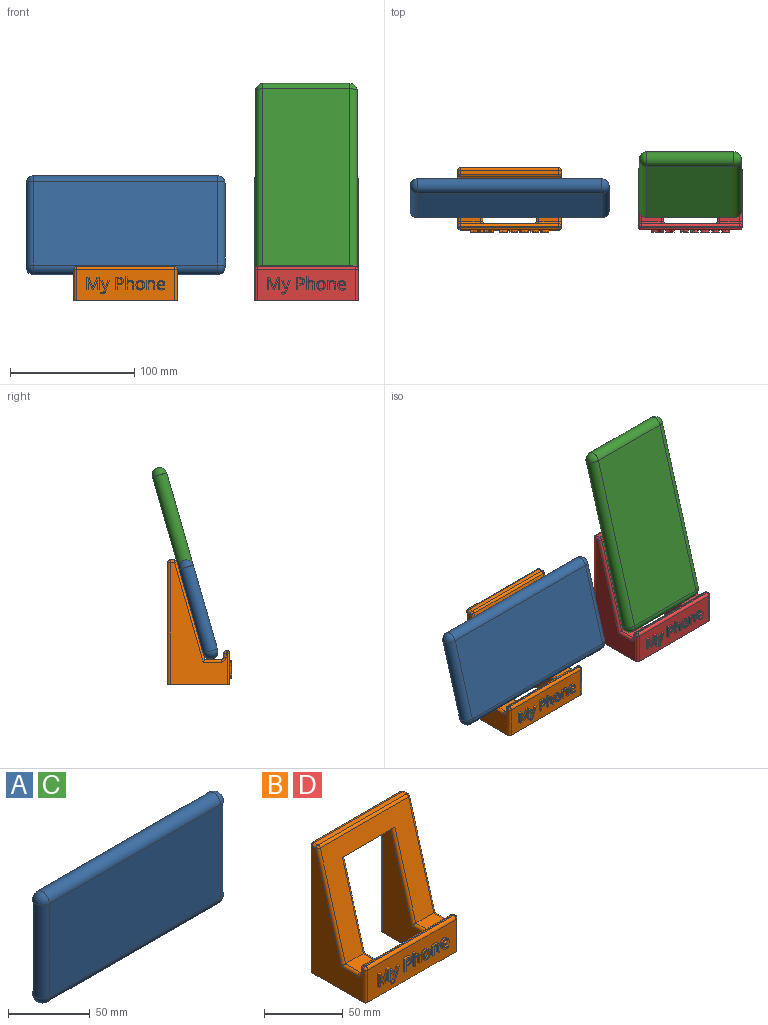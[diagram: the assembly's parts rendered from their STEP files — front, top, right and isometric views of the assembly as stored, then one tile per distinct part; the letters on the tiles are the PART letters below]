
ASSEMBLY  parts=4 mates=2
PART A: 10 faces, bbox 160x12x82 mm
  f0: plane 148x70mm, normal (0,-1,0), area 10360mm2, adj f3,f4,f7,f8
  f1: plane 148x70mm, normal (0,1,0), area 10360mm2, adj f3,f4,f7,f8
  f2: sphere r=6mm, area 113.1mm2, adj f3,f4
  f3: cylinder r=6mm len=148mm, axis (1,0,0), area 2789.7mm2, adj f0,f1,f2,f5
  f4: cylinder r=6mm len=70mm, axis (0,0,-1), area 1319.5mm2, adj f0,f1,f2,f6
  f5: sphere r=6mm, area 113.1mm2, adj f3,f7
  f6: sphere r=6mm, area 113.1mm2, adj f4,f8
  f7: cylinder r=6mm len=70mm, axis (0,0,1), area 1319.5mm2, adj f0,f1,f5,f9
  f8: cylinder r=6mm len=148mm, axis (-1,0,0), area 2789.7mm2, adj f0,f1,f6,f9
  f9: sphere r=6mm, area 113.1mm2, adj f7,f8
PART B: 184 faces, bbox 83x51.7x100 mm
  f0: plane 79x25mm, normal (0,-1,0), area 1757.8mm2, adj f2,f14,f15,f16,f17,f18,f19,f20
  f1: plane 16x13mm, normal (0,0,1), area 208mm2, adj f3,f175,f178,f181
  f2: plane 83x50mm, normal (0,0,-1), area 2211.6mm2, adj f0,f5,f6,f7,f10,f11,f12,f146
  f3: plane 79x78.55mm, normal (0,-0.96,0.28), area 3278.3mm2, adj f1,f4,f13,f144,f153,f165,f172,f174
  f4: plane 16x13mm, normal (0,0,1), area 208mm2, adj f3,f145,f151,f152
  f5: plane 98x79mm, normal (0,1,0), area 3747mm2, adj f2,f13,f147,f155,f156,f182,f183
  f6: plane 98x46mm, normal (1,0,0), area 2038mm2, adj f2,f156,f161,f166,f170,f172,f175,f176
  f7: plane 98x46mm, normal (-1,0,0), area 2038mm2, adj f2,f147,f149,f151,f153,f154,f158,f163
  f8: plane 79x3.49mm, normal (0,0,1), area 276mm2, adj f154,f155,f165,f166
  f9: plane 79x1mm, normal (0,0,1), area 79mm2, adj f162,f163,f170,f171
  f10: plane 79x25mm, normal (0,1,0), area 1101.9mm2, adj f2,f146,f150,f152,f164,f171,f176,f177
  f11: plane 85x41mm, normal (-1,0,0), area 1867.8mm2, adj f2,f13,f174,f177,f178,f183
  f12: plane 85x41mm, normal (1,0,0), area 1867.8mm2, adj f2,f13,f144,f145,f146,f182
  f13: plane 47x11.31mm, normal (0,0,-1), area 489.9mm2, adj f3,f5,f11,f12,f144,f174,f182,f183
  f14: plane 8.79x3.36mm, normal (-0.93,0,-0.36), area 16mm2, adj f0,f15,f31,f32
  f15: plane 1.7x0.93mm, normal (0,0,-1), area 1.6mm2, adj f0,f14,f16,f32
  f16: plane 8.78x3.39mm, normal (0.93,0,-0.36), area 16mm2, adj f0,f15,f17,f32
  f17: plane 1.7x0.05mm, normal (0,0,-1), area 0.1mm2, adj f0,f16,f18,f32
  f18: extruded ~2.39x1.7mm, area 4.1mm2, adj f0,f17,f19,f32
  f19: plane 6.39x1.7mm, normal (-1,0,0), area 10.9mm2, adj f0,f18,f20,f32
  f20: plane 1.7x1.15mm, normal (0,0,-1), area 2mm2, adj f0,f19,f21,f32
  f21: plane 9.92x1.7mm, normal (1,0,0), area 16.9mm2, adj f0,f20,f22,f32
  f22: plane 1.72x1.7mm, normal (0,0,1), area 2.9mm2, adj f0,f21,f23,f32
  f23: plane 8.18x3.17mm, normal (-0.93,0,0.36), area 14.9mm2, adj f0,f22,f24,f32
  f24: plane 1.7x0.05mm, normal (0,0,1), area 0.1mm2, adj f0,f23,f25,f32
  f25: plane 8.18x3.14mm, normal (0.93,0,0.36), area 14.9mm2, adj f0,f24,f26,f32
  f26: plane 1.74x1.7mm, normal (0,0,1), area 3mm2, adj f0,f25,f27,f32
  f27: plane 9.92x1.7mm, normal (-1,0,0), area 16.9mm2, adj f0,f26,f28,f32
  f28: plane 1.7x1.07mm, normal (0,0,-1), area 1.8mm2, adj f0,f27,f29,f32
  f29: plane 6.31x1.7mm, normal (1,0,0), area 10.7mm2, adj f0,f28,f30,f32
  f30: extruded ~2.48x1.7mm, area 4.2mm2, adj f0,f29,f31,f32
  f31: plane 1.7x0.05mm, normal (0,0,-1), area 0.1mm2, adj f0,f14,f30,f32
  f32: plane 9.92x9.82mm, normal (0,-1,0), area 42mm2, adj f14,f15,f16,f17,f18,f19,f20,f21
  f33: plane 1.7x1.21mm, normal (0,0,1), area 2.1mm2, adj f0,f34,f48,f49
  f34: plane 7.47x3mm, normal (-0.93,0,-0.37), area 13.7mm2, adj f0,f33,f35,f49
  f35: plane 1.7x1.06mm, normal (-0.93,0,0.37), area 1.9mm2, adj f0,f34,f36,f49
  f36: extruded ~1.7x1.66mm, area 3.8mm2, adj f0,f35,f37,f49
  f37: extruded ~1.7x0.83mm, area 1.4mm2, adj f0,f36,f38,f49
  f38: plane 1.7x0.9mm, normal (-1,0,0), area 1.5mm2, adj f0,f37,f39,f49
  f39: extruded ~1.7x1.02mm, area 1.7mm2, adj f0,f38,f40,f49
  f40: extruded ~1.7x1.56mm, area 2.9mm2, adj f0,f39,f41,f49
  f41: extruded ~1.78x1.7mm, area 3.6mm2, adj f0,f40,f42,f49
  f42: plane 8.46x3.19mm, normal (0.94,0,-0.35), area 15.4mm2, adj f0,f41,f43,f49
  f43: plane 1.7x1.21mm, normal (0,0,1), area 2.1mm2, adj f0,f42,f44,f49
  f44: extruded ~5.15x1.84mm, area 9.3mm2, adj f0,f43,f45,f49
  f45: extruded ~1.7x1.19mm, area 2.1mm2, adj f0,f44,f46,f49
  f46: plane 1.7x0.05mm, normal (0,0,1), area 0.1mm2, adj f0,f45,f47,f49
  f47: extruded ~2.1x1.7mm, area 3.7mm2, adj f0,f46,f48,f49
  f48: plane 4.24x1.7mm, normal (0.93,0,0.36), area 7.7mm2, adj f0,f33,f47,f49
  f49: plane 10.77x6.97mm, normal (0,-1,0), area 21.4mm2, adj f33,f34,f35,f36,f37,f38,f39,f40
  f50: plane 1.7x1.04mm, normal (0,0,1), area 1.8mm2, adj f51,f64,f65,f66
  f51: plane 4.03x1.7mm, normal (1,0,0), area 6.8mm2, adj f50,f52,f65,f66
  f52: plane 1.7x1.29mm, normal (0,0,-1), area 2.2mm2, adj f51,f53,f65,f66
  f53: extruded ~2.01x1.7mm, area 3.6mm2, adj f52,f54,f65,f66
  f54: extruded ~1.7x1.46mm, area 2.8mm2, adj f53,f55,f65,f66
  f55: extruded ~1.7x1.59mm, area 3.1mm2, adj f54,f64,f65,f66
  f56: extruded ~2.32x1.7mm, area 4.5mm2, adj f0,f57,f63,f65
  f57: extruded ~3.72x2.89mm, area 9.1mm2, adj f0,f56,f58,f65
  f58: plane 2.57x1.7mm, normal (0,0,1), area 4.4mm2, adj f0,f57,f59,f65
  f59: plane 9.92x1.7mm, normal (-1,0,0), area 16.9mm2, adj f0,f58,f60,f65
  f60: plane 1.7x1.15mm, normal (0,0,-1), area 2mm2, adj f0,f59,f61,f65
  f61: plane 3.9x1.7mm, normal (1,0,0), area 6.6mm2, adj f0,f60,f62,f65
  f62: plane 1.7x1.17mm, normal (0,0,-1), area 2mm2, adj f0,f61,f63,f65
  f63: extruded ~2.94x1.7mm, area 5.3mm2, adj f0,f56,f62,f65
  f64: extruded ~2.22x1.7mm, area 3.9mm2, adj f50,f55,f65,f66
  f65: plane 9.92x6.29mm, normal (0,-1,0), area 24.2mm2, adj f50,f51,f52,f53,f54,f55,f56,f57
  f66: plane 4.03x3.94mm, normal (0,-1,0), area 14.1mm2, adj f50,f51,f52,f53,f54,f55,f64
  f67: plane 4.81x1.7mm, normal (-1,0,0), area 8.2mm2, adj f0,f68,f84,f85
  f68: plane 1.7x1.13mm, normal (0,0,-1), area 1.9mm2, adj f0,f67,f69,f85
  f69: plane 4.85x1.7mm, normal (1,0,0), area 8.2mm2, adj f0,f68,f70,f85
  f70: extruded ~2.06x1.7mm, area 3.8mm2, adj f0,f69,f71,f85
  f71: extruded ~2.05x1.7mm, area 3.7mm2, adj f0,f70,f72,f85
  f72: extruded ~1.7x1.4mm, area 2.5mm2, adj f0,f71,f73,f85
  f73: extruded ~1.7x0.95mm, area 2.2mm2, adj f0,f72,f74,f85
  f74: plane 1.7x0.07mm, normal (0,0,1), area 0.1mm2, adj f0,f73,f75,f85
  f75: extruded ~1.7x0.96mm, area 1.6mm2, adj f0,f74,f76,f85
  f76: plane 3.19x1.7mm, normal (1,0,0), area 5.4mm2, adj f0,f75,f77,f85
  f77: plane 1.7x1.13mm, normal (0,0,1), area 1.9mm2, adj f0,f76,f78,f85
  f78: plane 10.55x1.7mm, normal (-1,0,0), area 17.9mm2, adj f0,f77,f79,f85
  f79: plane 1.7x1.13mm, normal (0,0,-1), area 1.9mm2, adj f0,f78,f80,f85
  f80: plane 3.89x1.7mm, normal (1,0,0), area 6.6mm2, adj f0,f79,f81,f85
  f81: extruded ~2.09x1.7mm, area 3.7mm2, adj f0,f80,f82,f85
  f82: extruded ~1.71x1.7mm, area 3.2mm2, adj f0,f81,f83,f85
  f83: extruded ~1.7x1.3mm, area 2.4mm2, adj f0,f82,f84,f85
  f84: extruded ~1.7x1.36mm, area 2.5mm2, adj f0,f67,f83,f85
  f85: plane 10.55x6.21mm, normal (0,-1,0), area 23.6mm2, adj f67,f68,f69,f70,f71,f72,f73,f74
  f86: extruded ~2.17x1.7mm, area 3.9mm2, adj f87,f102,f103,f104
  f87: extruded ~2.16x1.7mm, area 3.9mm2, adj f86,f88,f103,f104
  f88: extruded ~1.7x1.67mm, area 3.2mm2, adj f87,f89,f103,f104
  f89: extruded ~1.7x1.69mm, area 3.3mm2, adj f88,f90,f103,f104
  f90: extruded ~2.15x1.7mm, area 3.9mm2, adj f89,f91,f103,f104
  f91: extruded ~2.17x1.7mm, area 3.9mm2, adj f90,f92,f103,f104
  f92: extruded ~1.7x1.68mm, area 3.2mm2, adj f91,f102,f103,f104
  f93: extruded ~2.84x1.7mm, area 5.2mm2, adj f0,f94,f101,f103
  f94: extruded ~2.81x1.7mm, area 5.1mm2, adj f0,f93,f95,f103
  f95: extruded ~2.48x1.7mm, area 4.7mm2, adj f0,f94,f96,f103
  f96: extruded ~2.52x1.7mm, area 4.8mm2, adj f0,f95,f97,f103
  f97: extruded ~2.83x1.7mm, area 5.2mm2, adj f0,f96,f98,f103
  f98: extruded ~2.05x1.7mm, area 3.6mm2, adj f0,f97,f99,f103
  f99: extruded ~1.7x1.34mm, area 3.1mm2, adj f0,f98,f100,f103
  f100: extruded ~1.77x1.7mm, area 3.2mm2, adj f0,f99,f101,f103
  f101: extruded ~2.53x1.7mm, area 4.8mm2, adj f0,f93,f100,f103
  f102: extruded ~1.7x1.67mm, area 3.2mm2, adj f86,f92,f103,f104
  f103: plane 7.71x6.83mm, normal (0,-1,0), area 21.2mm2, adj f86,f87,f88,f89,f90,f91,f92,f93
  f104: plane 5.81x4.5mm, normal (0,-1,0), area 21.7mm2, adj f86,f87,f88,f89,f90,f91,f92,f102
  f105: plane 4.81x1.7mm, normal (-1,0,0), area 8.2mm2, adj f0,f106,f121,f122
  f106: plane 1.7x1.13mm, normal (0,0,-1), area 1.9mm2, adj f0,f105,f107,f122
  f107: plane 4.85x1.7mm, normal (1,0,0), area 8.2mm2, adj f0,f106,f108,f122
  f108: extruded ~2.07x1.7mm, area 3.8mm2, adj f0,f107,f109,f122
  f109: extruded ~2.02x1.7mm, area 3.7mm2, adj f0,f108,f110,f122
  f110: extruded ~1.7x1.39mm, area 2.4mm2, adj f0,f109,f111,f122
  f111: extruded ~1.7x0.97mm, area 2.2mm2, adj f0,f110,f112,f122
  f112: plane 1.7x0.05mm, normal (0,0,1), area 0.1mm2, adj f0,f111,f113,f122
  f113: plane 1.7x1.02mm, normal (0.98,0,0.18), area 1.8mm2, adj f0,f112,f114,f122
  f114: plane 1.7x0.92mm, normal (0,0,1), area 1.6mm2, adj f0,f113,f115,f122
  f115: plane 7.43x1.7mm, normal (-1,0,0), area 12.6mm2, adj f0,f114,f116,f122
  f116: plane 1.7x1.13mm, normal (0,0,-1), area 1.9mm2, adj f0,f115,f117,f122
  f117: plane 3.9x1.7mm, normal (1,0,0), area 6.6mm2, adj f0,f116,f118,f122
  f118: extruded ~2.08x1.7mm, area 3.7mm2, adj f0,f117,f119,f122
  f119: extruded ~1.71x1.7mm, area 3.2mm2, adj f0,f118,f120,f122
  f120: extruded ~1.7x1.3mm, area 2.4mm2, adj f0,f119,f121,f122
  f121: extruded ~1.7x1.36mm, area 2.5mm2, adj f0,f105,f120,f122
  f122: plane 7.57x6.21mm, normal (0,-1,0), area 20mm2, adj f105,f106,f107,f108,f109,f110,f111,f112
  f123: extruded ~1.7x1.43mm, area 2.7mm2, adj f124,f141,f142,f143
  f124: extruded ~1.7x1.36mm, area 2.6mm2, adj f123,f125,f142,f143
  f125: extruded ~1.7x1.63mm, area 2.9mm2, adj f124,f126,f142,f143
  f126: plane 3.89x1.7mm, normal (0,0,1), area 6.6mm2, adj f125,f141,f142,f143
  f127: extruded ~2.6x1.7mm, area 4.9mm2, adj f0,f128,f140,f142
  f128: extruded ~1.7x1.28mm, area 2.2mm2, adj f0,f127,f129,f142
  f129: extruded ~1.7x1.13mm, area 2mm2, adj f0,f128,f130,f142
  f130: plane 1.7x1mm, normal (1,0,0), area 1.7mm2, adj f0,f129,f131,f142
  f131: extruded ~2.37x1.7mm, area 4.2mm2, adj f0,f130,f132,f142
  f132: extruded ~1.77x1.7mm, area 3.3mm2, adj f0,f131,f133,f142
  f133: extruded ~1.99x1.7mm, area 3.6mm2, adj f0,f132,f134,f142
  f134: plane 5.12x1.7mm, normal (0,0,-1), area 8.7mm2, adj f0,f133,f135,f142
  f135: plane 1.7x0.71mm, normal (1,0,0), area 1.2mm2, adj f0,f134,f136,f142
  f136: extruded ~2.43x1.7mm, area 4.4mm2, adj f0,f135,f137,f142
  f137: extruded ~2.21x1.7mm, area 4.2mm2, adj f0,f136,f138,f142
  f138: extruded ~2.38x1.7mm, area 4.6mm2, adj f0,f137,f139,f142
  f139: extruded ~2.86x1.7mm, area 5.2mm2, adj f0,f138,f140,f142
  f140: extruded ~2.79x1.7mm, area 5.1mm2, adj f0,f127,f139,f142
  f141: extruded ~1.7x1.61mm, area 3mm2, adj f123,f126,f142,f143
  f142: plane 7.71x6.29mm, normal (0,-1,0), area 22mm2, adj f123,f124,f125,f126,f127,f128,f129,f130
  f143: plane 3.89x2.2mm, normal (0,-1,0), area 6.9mm2, adj f123,f124,f125,f126,f141
  f144: cylinder r=2mm len=67.55mm, axis (0,0.28,0.96), area 214.9mm2, adj f3,f12,f13,f145
  f145: cylinder r=2mm len=14.51mm, axis (0,1,0), area 42.6mm2, adj f4,f12,f144,f150
  f146: cylinder r=2mm len=18mm, axis (0,0,-1), area 56.5mm2, adj f2,f10,f12,f150
  f147: cylinder r=2mm len=98mm, axis (0,0,1), area 307.9mm2, adj f2,f5,f7,f148
  f148: sphere r=2mm, area 6.3mm2, adj f147,f154,f155
  f149: cylinder r=2mm len=25mm, axis (0,0,-1), area 78.5mm2, adj f0,f2,f7,f157
  f150: torus R=4mm, axis (0,-1,0), area 13.5mm2, adj f10,f145,f146,f152
  f151: cylinder r=2mm len=14.51mm, axis (0,-1,0), area 42.6mm2, adj f4,f7,f153,f158
  f152: cylinder r=2mm len=16mm, axis (1,0,0), area 50.3mm2, adj f4,f10,f150,f158
  f153: cylinder r=2mm len=80.55mm, axis (0,-0.28,-0.96), area 258.5mm2, adj f3,f7,f151,f159
  f154: cylinder r=2mm len=3.49mm, axis (0,-1,0), area 11mm2, adj f7,f8,f148,f159
  f155: cylinder r=2mm len=79mm, axis (-1,0,0), area 248.2mm2, adj f5,f8,f148,f160
  f156: cylinder r=2mm len=98mm, axis (0,0,-1), area 307.9mm2, adj f2,f5,f6,f160
  f157: sphere r=2mm, area 6.3mm2, adj f149,f162,f163
  f158: torus R=4mm, axis (1,0,0), area 13.5mm2, adj f7,f151,f152,f164
  f159: sphere r=2mm, area 5.2mm2, adj f153,f154,f165
  f160: sphere r=2mm, area 6.3mm2, adj f155,f156,f166
  f161: cylinder r=2mm len=25mm, axis (0,0,1), area 78.5mm2, adj f0,f2,f6,f167
  f162: cylinder r=2mm len=79mm, axis (-1,0,0), area 248.2mm2, adj f0,f9,f157,f167
  f163: cylinder r=2mm len=2mm, axis (0,-1,0), area 3.1mm2, adj f7,f9,f157,f168
  f164: cylinder r=2mm len=3mm, axis (0,0,1), area 9.4mm2, adj f7,f10,f158,f168
  f165: cylinder r=2mm len=79mm, axis (-1,0,0), area 204mm2, adj f3,f8,f159,f169
  f166: cylinder r=2mm len=3.49mm, axis (0,1,0), area 11mm2, adj f6,f8,f160,f169
  f167: sphere r=2mm, area 6.3mm2, adj f161,f162,f170
  f168: sphere r=2mm, area 6.3mm2, adj f163,f164,f171
  f169: sphere r=2mm, area 5.2mm2, adj f165,f166,f172
  f170: cylinder r=2mm len=2mm, axis (0,1,0), area 3.1mm2, adj f6,f9,f167,f173
  f171: cylinder r=2mm len=79mm, axis (1,0,0), area 248.2mm2, adj f9,f10,f168,f173
  f172: cylinder r=2mm len=80.55mm, axis (0,0.28,0.96), area 258.5mm2, adj f3,f6,f169,f175
  f173: sphere r=2mm, area 6.3mm2, adj f170,f171,f176
  f174: cylinder r=2mm len=67.55mm, axis (0,-0.28,-0.96), area 214.9mm2, adj f3,f11,f13,f178
  f175: cylinder r=2mm len=14.51mm, axis (0,1,0), area 42.6mm2, adj f1,f6,f172,f179
  f176: cylinder r=2mm len=3mm, axis (0,0,-1), area 9.4mm2, adj f6,f10,f173,f179
  f177: cylinder r=2mm len=18mm, axis (0,0,1), area 56.5mm2, adj f2,f10,f11,f180
  f178: cylinder r=2mm len=14.51mm, axis (0,-1,0), area 42.6mm2, adj f1,f11,f174,f180
  f179: torus R=4mm, axis (1,0,0), area 13.5mm2, adj f6,f175,f176,f181
  f180: torus R=4mm, axis (0,-1,0), area 13.5mm2, adj f10,f177,f178,f181
  f181: cylinder r=2mm len=16mm, axis (1,0,0), area 50.3mm2, adj f1,f10,f179,f180
  f182: cylinder r=2mm len=85mm, axis (0,0,1), area 267mm2, adj f2,f5,f12,f13
  f183: cylinder r=2mm len=85mm, axis (0,0,-1), area 267mm2, adj f2,f5,f11,f13
PART C: same geometry as A
PART D: same geometry as B
PLACE A rot(axis=(-1,0,0),16deg) t=(-39.91,-5.17,2.31)mm
PLACE B t=(-39.91,25.01,-17.05)mm
PLACE C rot(axis=(-0.14,0.98,-0.14),91.1deg) t=(64.38,16.85,78.51)mm
PLACE D t=(105.38,25.09,-17.15)mm
MATE planar C.f1 <-> D.f3  axis (0,0.96,-0.28) through (105.38,16.85,78.51)mm
MATE planar A.f1 <-> B.f3  axis (0,0.96,-0.28) through (-39.91,6.15,41.71)mm
